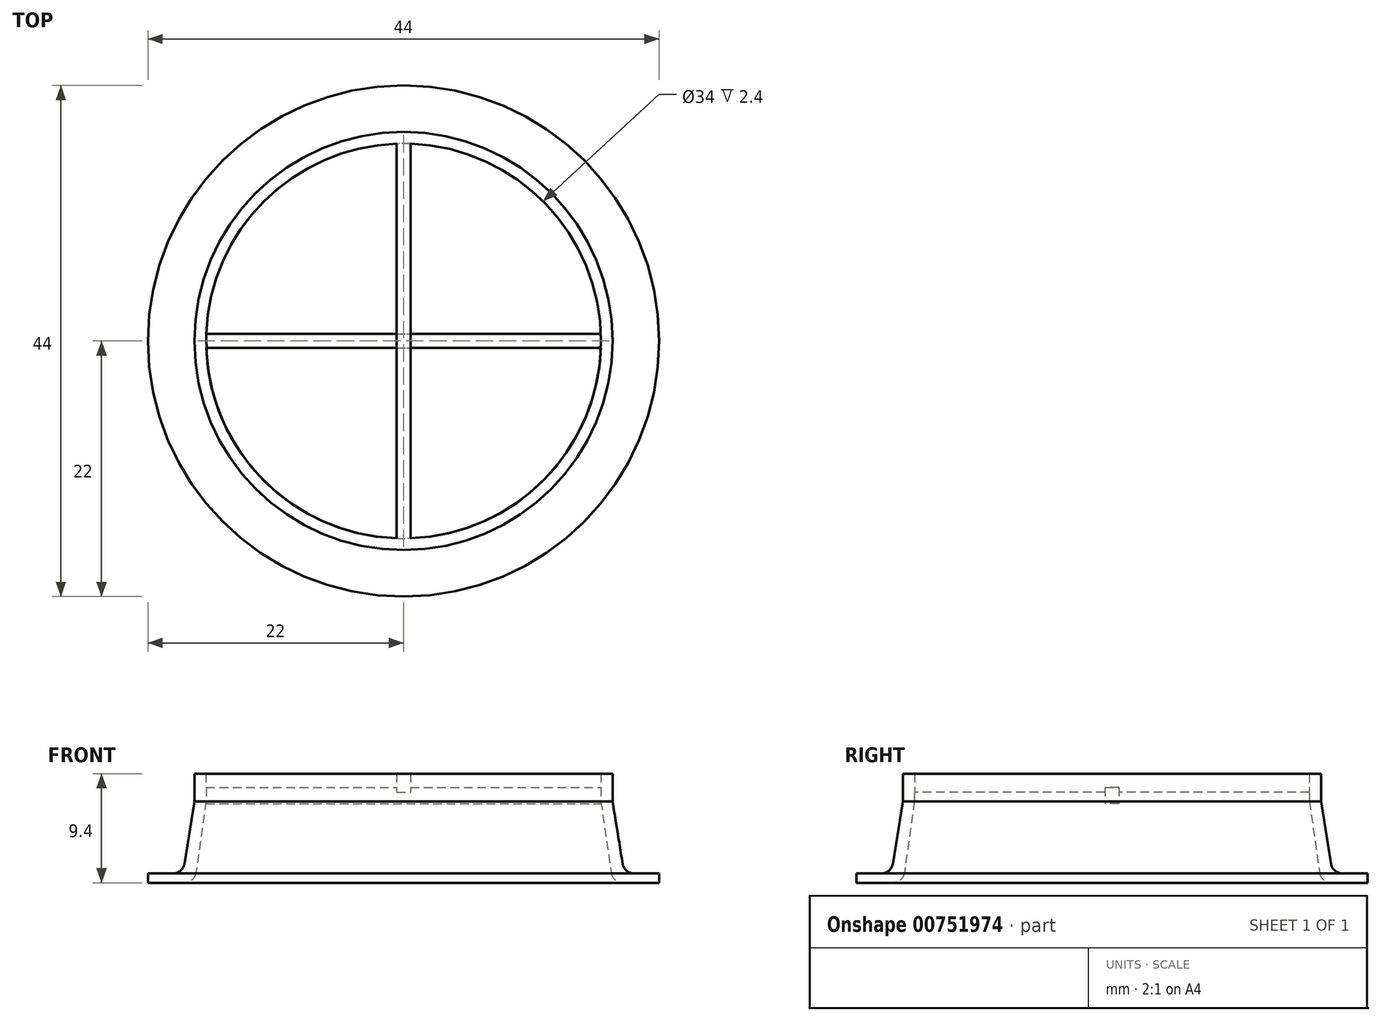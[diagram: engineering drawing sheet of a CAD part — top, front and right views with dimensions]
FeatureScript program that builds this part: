
annotation { "Feature Type Name" : "Feature", "Feature Type Description" : "" }
export const myFeature = defineFeature(function(context is Context, id is Id, definition is map)
    precondition{}
    {
        {
            var Q0;
            Q0=qCreatedBy(makeId("Front.planeOp"),FACE);
            var sketch = newSketch(context, id + "F0", { "sketchPlane" : qUnion([Q0])});
            skLineSegment(sketch, "E0", {"start": v(0, 16.66) * mm, "end": v(0, -15.75) * mm, "construction": true});
            skLineSegment(sketch, "E1", {"start": v(8.08, 0) * mm, "end": v(-29.3, 0) * mm, "construction": true});
            skLineSegment(sketch, "E2", {"start": v(1.58, 0) * mm, "end": v(-1.66, 0) * mm, "construction": true});
            skLineSegment(sketch, "E3", {"start": v(-1, 1.45) * mm, "end": v(-1, -7.95) * mm, "construction": true});
            skLineSegment(sketch, "E4", {"start": v(-5, -6.2) * mm, "end": v(-5, -8.06) * mm, "construction": true});
            skLineSegment(sketch, "E5", {"start": v(-5, -7) * mm, "end": v(-1.87, -7) * mm});
            skLineSegment(sketch, "E6", {"start": v(-0.88, -6.14) * mm, "end": v(0, 0) * mm});
            skLineSegment(sketch, "E7", {"start": v(0, 0) * mm, "end": v(-1, 0) * mm});
            skLineSegment(sketch, "E8", {"start": v(-1, 0) * mm, "end": v(-1.86, -5.36) * mm});
            skLineSegment(sketch, "E9", {"start": v(-2.85, -6.2) * mm, "end": v(-5, -6.2) * mm});
            skLineSegment(sketch, "E10", {"start": v(-5, -6.2) * mm, "end": v(-5, -7) * mm});
            skPoint(sketch, "E11.visualSharp", {"position": v(-2, -6.2) * mm});
            skArc(sketch, "E11.filletArc", {"start": v(-2.85, -6.2) * mm, "mid": v(-2.2, -5.96) * mm, "end": v(-1.86, -5.36) * mm});
            skPoint(sketch, "E12.visualSharp", {"position": v(-1, -7) * mm});
            skArc(sketch, "E12.filletArc", {"start": v(-1.87, -7) * mm, "mid": v(-1.21, -6.76) * mm, "end": v(-0.88, -6.14) * mm});
            skLineSegment(sketch, "E13", {"start": v(17, 0.36) * mm, "end": v(17, -7.36) * mm, "construction": true});
            skSolve(sketch);
        }
        {
            var Q0;
            Q0=qSketchRegion(id+"F0",true);
            var Q1;
            Q1=sQuery(id+"F0.wireOp",EDGE,"E13");
            revolve(context, id + "F1", {"surfaceOperationType" : NewSurfaceOperationType.NEW, "entities" : qUnion([Q0]), "axis" : qUnion([Q1]), "revolveType" : RevolveType.FULL});
        }
        {
            var Q0;
            Q0=makeQuery(id+"F1.opRevolve","SWEPT_FACE",FACE,{"disambiguationData":[OSD([sQuery(id+"F0.wireOp",EDGE,"E7")])]});
            var sketch = newSketch(context, id + "F2", { "sketchPlane" : qUnion([Q0])});
            skLineSegment(sketch, "E14", {"start": v(0, 0) * mm, "end": v(34, 0) * mm, "construction": true});
            skCircle(sketch, "E15.0", {"center": v(17, 0) * mm, "radius": 18 * mm});
            skLineSegment(sketch, "E16", {"start": v(-0.99, 0.6) * mm, "end": v(34.99, 0.6) * mm});
            skLineSegment(sketch, "E17.MirrorCS", {"start": v(-0.99, -0.6) * mm, "end": v(34.99, -0.6) * mm});
            skSolve(sketch);
        }
        {
            var Q0;
            {var subQ0=sQuery(id+"F2.wireOp",EDGE,"GnbASiE2-4hr6-BGUo-1MwE-UTMWuamxon4s");var subQ1=makeQuery(id+"F1.opRevolve","SWEPT_EDGE",EDGE,{"disambiguationData":[OSD([sQuery(id+"F0.wireOp",EDGE,"E6"),sQuery(id+"F0.wireOp",EDGE,"E7")])]});var subQ2=makeQuery(id+"F2.imprint","INTERSECT",VERTEX,{"disambiguationData":[OD(0.0)],"derivedFrom":[subQ1,subQ0]});Q0=makeQuery(id+"F2.imprint","IMPRINT",FACE,{"disambiguationData":[TD([[makeQuery(id+"F2.imprint","IMPRINT",EDGE,{"disambiguationData":[TD([[subQ2,-1.0]])],"derivedFrom":subQ0}),1.0]])]});}
            var Q1;
            {var subQ0=sQuery(id+"F2.wireOp",EDGE,"E16");var subQ1=makeQuery(id+"F1.opRevolve","SWEPT_EDGE",EDGE,{"disambiguationData":[OSD([sQuery(id+"F0.wireOp",EDGE,"E6"),sQuery(id+"F0.wireOp",EDGE,"E7")])]});var subQ2=makeQuery(id+"F2.imprint","INTERSECT",VERTEX,{"disambiguationData":[OD(0.0)],"derivedFrom":[subQ1,subQ0]});Q1=makeQuery(id+"F2.imprint","IMPRINT",FACE,{"disambiguationData":[TD([[makeQuery(id+"F2.imprint","IMPRINT",EDGE,{"disambiguationData":[TD([[subQ2,-1.0]])],"derivedFrom":subQ0}),-1.0]])]});}
            var Q2;
            {var subQ0=sQuery(id+"F2.wireOp",EDGE,"c4f6b68d-a1a1-4662-875f-d93fe2d7bfcd0.MirrorCS");var subQ1=makeQuery(id+"F1.opRevolve","SWEPT_EDGE",EDGE,{"disambiguationData":[OSD([sQuery(id+"F0.wireOp",EDGE,"E6"),sQuery(id+"F0.wireOp",EDGE,"E7")])]});var subQ2=makeQuery(id+"F2.imprint","INTERSECT",VERTEX,{"disambiguationData":[OD(0.0)],"derivedFrom":[subQ1,subQ0]});Q2=makeQuery(id+"F2.imprint","IMPRINT",FACE,{"disambiguationData":[TD([[makeQuery(id+"F2.imprint","IMPRINT",EDGE,{"disambiguationData":[TD([[subQ2,-1.0]])],"derivedFrom":subQ0}),-1.0]])]});}
            extrude(context, id + "F3", {"entities" : qUnion([Q0, Q1, Q2]), "depth" : 1.2 * mm, "offsetDistance" : 25 * mm, "hasSecondDirection" : true, "secondDirectionOppositeDirection" : true, "secondDirectionDepth" : .2 * mm});
        }
        {
            var Q0;
            Q0=makeQuery(id+"F1.opRevolve","SWEPT_FACE",FACE,{"disambiguationData":[OSD([sQuery(id+"F0.wireOp",EDGE,"E7")])]});
            var sketch = newSketch(context, id + "F4", { "sketchPlane" : qUnion([Q0])});
            skCircle(sketch, "E18.0", {"center": v(17, 0) * mm, "radius": 17 * mm});
            skCircle(sketch, "E19.0", {"center": v(17, 0) * mm, "radius": 18 * mm});
            skSolve(sketch);
        }
        {
            var Q0;
            Q0=qSketchRegion(id+"F4",true);
            extrude(context, id + "F5", {"entities" : qUnion([Q0]), "depth" : 1.2 * mm, "offsetDistance" : 25 * mm});
        }
        {
            var Q0;
            Q0=makeQuery(id+"F5.opExtrude","CAP_FACE",FACE,{"disambiguationData":[OSD([sQuery(id+"F4.wireOp",EDGE,"E18.0"),sQuery(id+"F4.wireOp",EDGE,"E19.0")])],"isStart":false});
            var sketch = newSketch(context, id + "F6", { "sketchPlane" : qUnion([Q0])});
            skLineSegment(sketch, "E20", {"start": v(17, 17) * mm, "end": v(17, -17) * mm, "construction": true});
            skLineSegment(sketch, "E21", {"start": v(17.6, 16.99) * mm, "end": v(17.6, -16.99) * mm});
            skLineSegment(sketch, "E22.MirrorCS", {"start": v(16.4, 16.99) * mm, "end": v(16.4, -16.99) * mm});
            skCircle(sketch, "E23.0", {"center": v(17, 0) * mm, "radius": 18 * mm});
            skCircle(sketch, "E24.0", {"center": v(17, 0) * mm, "radius": 17 * mm});
            skLineSegment(sketch, "E25", {"start": v(7.19, 13.88) * mm, "end": v(7.99, 14.41) * mm});
            skLineSegment(sketch, "E26", {"start": v(26.01, 14.41) * mm, "end": v(26.81, 13.88) * mm});
            skLineSegment(sketch, "E27", {"start": v(26.81, -13.88) * mm, "end": v(26.01, -14.41) * mm});
            skLineSegment(sketch, "E28", {"start": v(7.99, -14.41) * mm, "end": v(7.19, -13.88) * mm});
            skSolve(sketch);
        }
        {
            var Q0;
            Q0=qSketchRegion(id+"F6",true);
            var Q1;
            Q1=makeQuery(id+"F6.imprint","IMPRINT",FACE,{"disambiguationData":[TD([[makeQuery(id+"F6.imprint","IMPRINT",EDGE,{"derivedFrom":sQuery(id+"F6.wireOp",EDGE,"c989af30-8120-479b-a04d-98639001230f0.MirrorCS")}),-1.0]])]});
            var Q2;
            Q2=makeQuery(id+"F6.imprint","IMPRINT",FACE,{"disambiguationData":[TD([[makeQuery(id+"F6.imprint","IMPRINT",EDGE,{"derivedFrom":sQuery(id+"F6.wireOp",EDGE,"E21")}),-1.0]])]});
            var Q3;
            Q3=makeQuery(id+"F6.imprint","IMPRINT",FACE,{"disambiguationData":[TD([[makeQuery(id+"F6.imprint","IMPRINT",EDGE,{"derivedFrom":sQuery(id+"F6.wireOp",EDGE,"oEIsb450-emK3-YmeS-2kUq-3WLzpkzzBy3d")}),1.0]])]});
            extrude(context, id + "F7", {"entities" : qUnion([Q0, Q1, Q2, Q3]), "operationType" : NewBodyOperationType.ADD, "depth" : 1.2 * mm, "offsetDistance" : 25 * mm, "hasSecondDirection" : true, "secondDirectionOppositeDirection" : true, "secondDirectionDepth" : .4 * mm});
        }
    });
